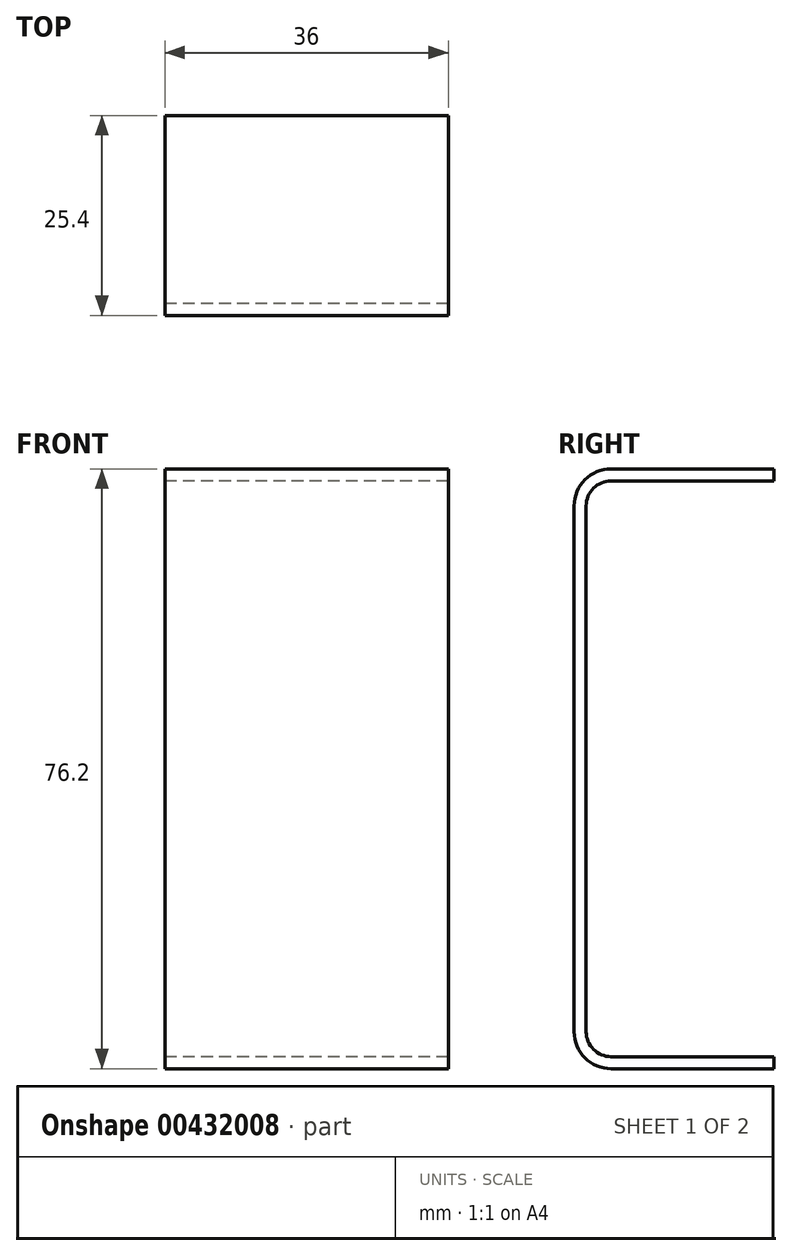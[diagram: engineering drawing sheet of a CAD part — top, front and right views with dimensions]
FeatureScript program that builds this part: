
annotation { "Feature Type Name" : "Feature", "Feature Type Description" : "" }
export const myFeature = defineFeature(function(context is Context, id is Id, definition is map)
    precondition{}
    {
        {
            assignVariable(context, id + "F0", {"name" : "length", "anyValue" : 36});
        }
        {
            var Q0;
            Q0=qCreatedBy(makeId("Right.planeOp"),FACE);
            var sketch = newSketch(context, id + "F1", { "sketchPlane" : qUnion([Q0])});
            skLineSegment(sketch, "E0", {"start": v(0, 4.7) * mm, "end": v(0, 71.5) * mm});
            skLineSegment(sketch, "E1", {"start": v(4.7, 76.2) * mm, "end": v(25.4, 76.2) * mm});
            skLineSegment(sketch, "E2", {"start": v(4.7, 0) * mm, "end": v(25.4, 0) * mm});
            skPoint(sketch, "E3.visualSharp", {"position": v(0, 76.2) * mm});
            skArc(sketch, "E3.filletArc", {"start": v(4.7, 76.2) * mm, "mid": v(1.38, 74.82) * mm, "end": v(0, 71.5) * mm});
            skPoint(sketch, "E4.visualSharp", {"position": v(0, 0) * mm});
            skArc(sketch, "E4.filletArc", {"start": v(0, 4.7) * mm, "mid": v(1.38, 1.38) * mm, "end": v(4.7, 0) * mm});
            skLineSegment(sketch, "E5.0", {"start": v(4.7, 1.52) * mm, "end": v(25.4, 1.52) * mm});
            skLineSegment(sketch, "E5.1", {"start": v(4.7, 74.68) * mm, "end": v(25.4, 74.68) * mm});
            skArc(sketch, "E5.2", {"start": v(4.7, 74.68) * mm, "mid": v(2.45, 73.75) * mm, "end": v(1.52, 71.5) * mm});
            skLineSegment(sketch, "E5.3", {"start": v(1.52, 4.7) * mm, "end": v(1.52, 71.5) * mm});
            skArc(sketch, "E5.4", {"start": v(1.52, 4.7) * mm, "mid": v(2.45, 2.45) * mm, "end": v(4.7, 1.52) * mm});
            skLineSegment(sketch, "E6", {"start": v(25.4, 76.2) * mm, "end": v(25.4, 74.68) * mm});
            skLineSegment(sketch, "E7", {"start": v(25.4, 1.52) * mm, "end": v(25.4, 0) * mm});
            skSolve(sketch);
        }
        {
            var Q0;
            Q0 = qSketchRegion(id + "F1", true);
            extrude(context, id + "F2", {"entities" : qUnion([Q0]), "endBound" : BoundingType.SYMMETRIC, "depth" : (getVariable(context, 'length')) * mm});
        }
        {
            var Q0;
            Q0=makeQuery(id+"F2.opExtrude","SWEPT_FACE",FACE,{"disambiguationData":[OSD([sQuery(id+"F1.wireOp",EDGE,"E0")])]});
            var sketch = newSketch(context, id + "F3", { "sketchPlane" : qUnion([Q0])});
            skCircle(sketch, "E8", {"center": v(-444.5, 63.5) * mm, "radius": 3.97 * mm});
            skCircle(sketch, "E9", {"center": v(-444.5, 12.7) * mm, "radius": 3.97 * mm});
            skLineSegment(sketch, "E10", {"start": v(-579.32, 38.1) * mm, "end": v(-457.2, 38.1) * mm, "construction": true});
            skSolve(sketch);
        }
        {
            var Q0;
            Q0 = qSketchRegion(id + "F3", true);
            extrude(context, id + "F4", {"entities" : qUnion([Q0]), "operationType" : NewBodyOperationType.REMOVE, "endBound" : BoundingType.THROUGH_ALL, "oppositeDirection" : true, "depth" : 25.4 * mm});
        }
    });
